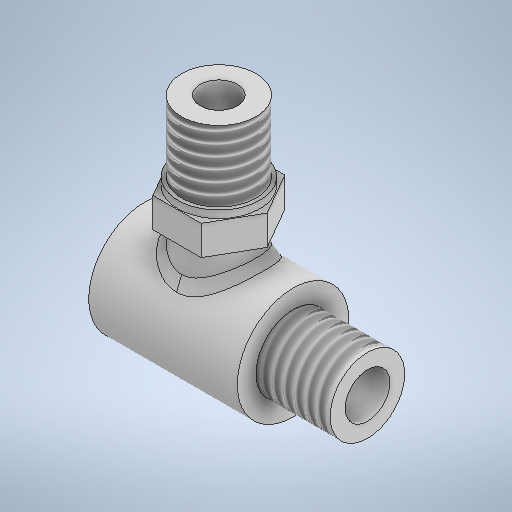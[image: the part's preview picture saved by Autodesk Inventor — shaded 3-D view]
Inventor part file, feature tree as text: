
AUTODESK INVENTOR PART (.ipt)
format: ipt  version: 2025.1 (Build 291241000, 241)  size: 390,656 bytes
history: native  units: mm
features: sketch x7, extrude x3, hole x3, thread x3, plane x2, projected_geometry x2, revolve x1, chamfer x1
ambient origin geometry x8: Origin, YZ Plane, XZ Plane, XY Plane, X Axis, Y Axis, Z Axis, Center Point
bodies: Solid1 (feature_tree)
feature tree (22):
  revolve  "Revolution1"  [1 undecoded]
  plane  "Work Plane1"
  extrude  "Extrusion1"  Depth=10.0mm
  plane  "Work Plane2"
  extrude  "Extrusion2"  Depth=25.0mm
  chamfer  "Chamfer1"  Distance=10.0mm
  hole  "Hole1"  [1 undecoded]
  hole  "Hole2"  [1 undecoded]
  hole  "Hole3"  [1 undecoded]
  thread  "Thread2"  [1 undecoded]
  extrude  "Extrusion3"  Depth=4.0mm
  thread  "Thread3"  [1 undecoded]
  thread  "Thread4"  [1 undecoded]
  sketch  "Sketch1"  dims[d0=30.0mm d1=10.0mm]
  sketch  "Sketch2"  dims[d2=15.0mm d3=10.0mm]
  sketch  "Sketch3"  dims[d4=90.0deg d5=25.0mm]
  projected_geometry  "Projected Loop1"
  sketch  "Sketch4"  dims[d6=10.0mm]
  sketch  "Sketch5"  dims[d7=10.0mm d8=10.0mm d9=0.0mm]
  sketch  "Sketch6"  dims[d10=12.5mm d11=13.0mm]
  sketch  "Sketch7"  dims[d12=10.0mm d13=4.0mm d14=0.0mm d17=1.0mm d18=2.0mm d19=45.0deg d20=5.0mm d21=6.0mm d22=4.0mm d23=2.0mm d24=90.0deg d25=25.0mm d26=0.0mm d27=8.0mm d28=6.0mm d29=4.0mm d30=2.0mm d31=90.0deg d32=16.0mm d33=0.0mm d34=6.0mm d35=6.0mm d36=4.0mm d37=2.0mm d38=90.0deg d39=14.0mm d40=0.0mm d41=9.0mm d42=0.0mm d43=11.0mm d44=1.0mm d45=0.0mm d46=9.5mm d47=0.0mm d48=9.5mm d49=0.0mm]
  projected_geometry  "Project Cut Edges1"
note: 7 required parameter values undecoded (feature->parameter linkage not recoverable at this tier; creation-order binding heuristic only, values carry confidence <= 0.55)